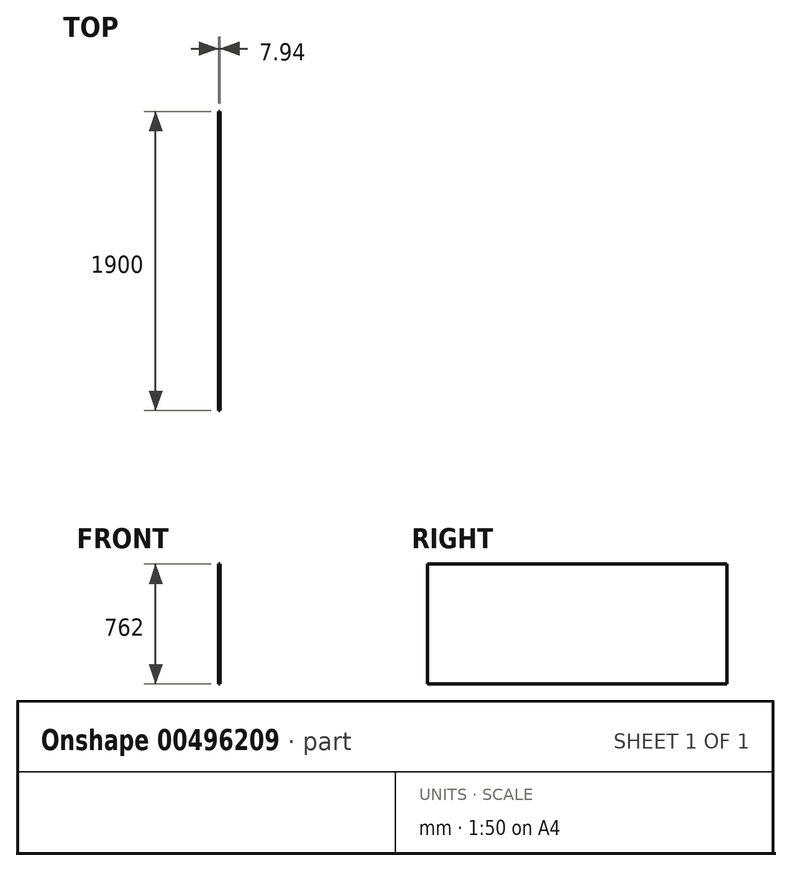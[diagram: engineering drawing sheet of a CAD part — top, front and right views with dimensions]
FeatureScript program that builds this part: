
annotation { "Feature Type Name" : "Feature", "Feature Type Description" : "" }
export const myFeature = defineFeature(function(context is Context, id is Id, definition is map)
    precondition{}
    {
        {
            var Q0;
            Q0=qCreatedBy(makeId("Right.planeOp"),FACE);
            var sketch = newSketch(context, id + "F0", { "sketchPlane" : qUnion([Q0])});
            skLineSegment(sketch, "E0.bottom", {"start": v(0, 0) * mm, "end": v(-1900, 0) * mm});
            skLineSegment(sketch, "E0.top", {"start": v(0, 762) * mm, "end": v(-1900, 762) * mm});
            skLineSegment(sketch, "E0.left", {"start": v(0, 0) * mm, "end": v(0, 762) * mm});
            skLineSegment(sketch, "E0.right", {"start": v(-1900, 0) * mm, "end": v(-1900, 762) * mm});
            skSolve(sketch);
        }
        {
            var Q0;
            Q0 = qSketchRegion(id + "F0", true);
            extrude(context, id + "F1", {"entities" : qUnion([Q0]), "depth" : 7.94 * mm, "offsetDistance" : 25.4 * mm});
        }
    });
